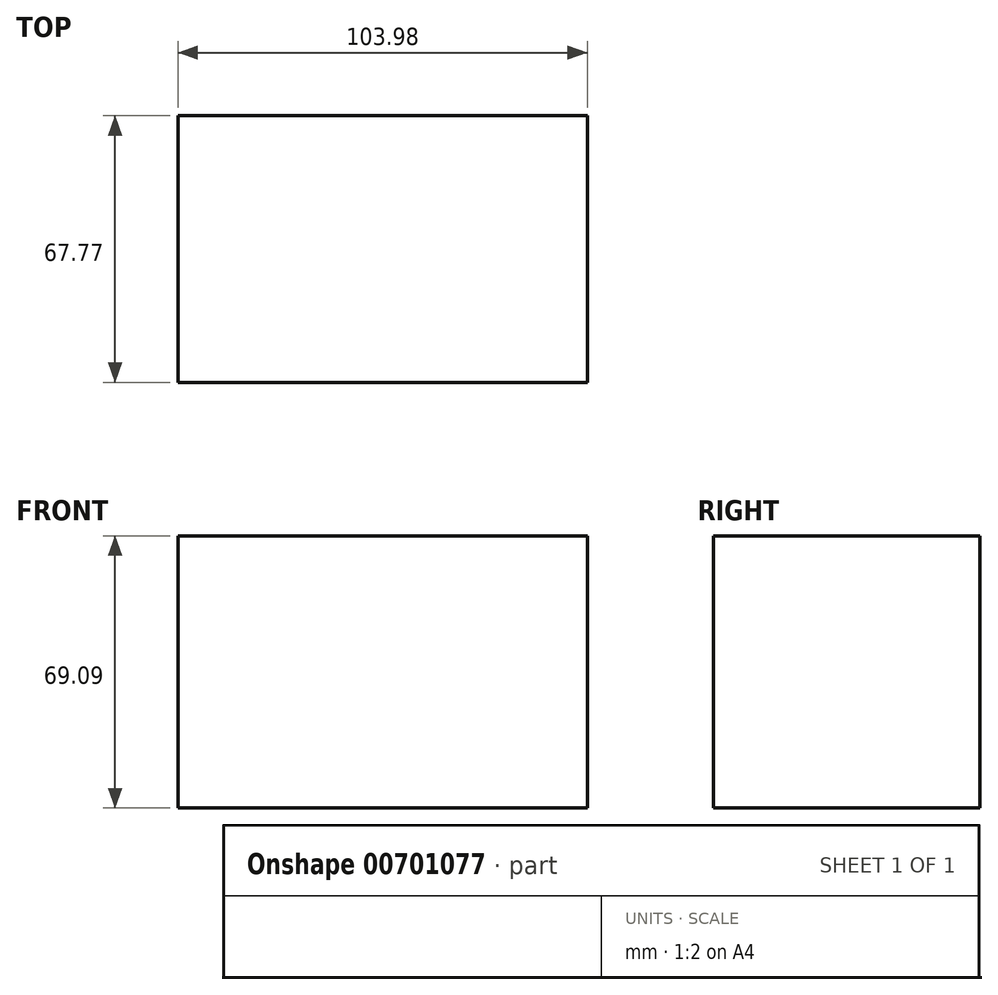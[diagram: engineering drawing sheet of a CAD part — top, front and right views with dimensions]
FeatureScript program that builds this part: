
annotation { "Feature Type Name" : "Feature", "Feature Type Description" : "" }
export const myFeature = defineFeature(function(context is Context, id is Id, definition is map)
    precondition{}
    {
        {
            var Q0;
            Q0=qCreatedBy(makeId("Top.planeOp"),FACE);
            var sketch = newSketch(context, id + "F0", { "sketchPlane" : qUnion([Q0])});
            skLineSegment(sketch, "E0.bottom", {"start": v(-69.24, -28.37) * mm, "end": v(34.74, -28.37) * mm});
            skLineSegment(sketch, "E0.top", {"start": v(-69.24, 39.4) * mm, "end": v(34.74, 39.4) * mm});
            skLineSegment(sketch, "E0.left", {"start": v(-69.24, -28.37) * mm, "end": v(-69.24, 39.4) * mm});
            skLineSegment(sketch, "E0.right", {"start": v(34.74, -28.37) * mm, "end": v(34.74, 39.4) * mm});
            skSolve(sketch);
        }
        {
            var Q0;
            Q0 = qSketchRegion(id + "F0", true);
            extrude(context, id + "F1", {"entities" : qUnion([Q0]), "depth" : 69.1 * mm, "offsetDistance" : 25.4 * mm});
        }
    });
